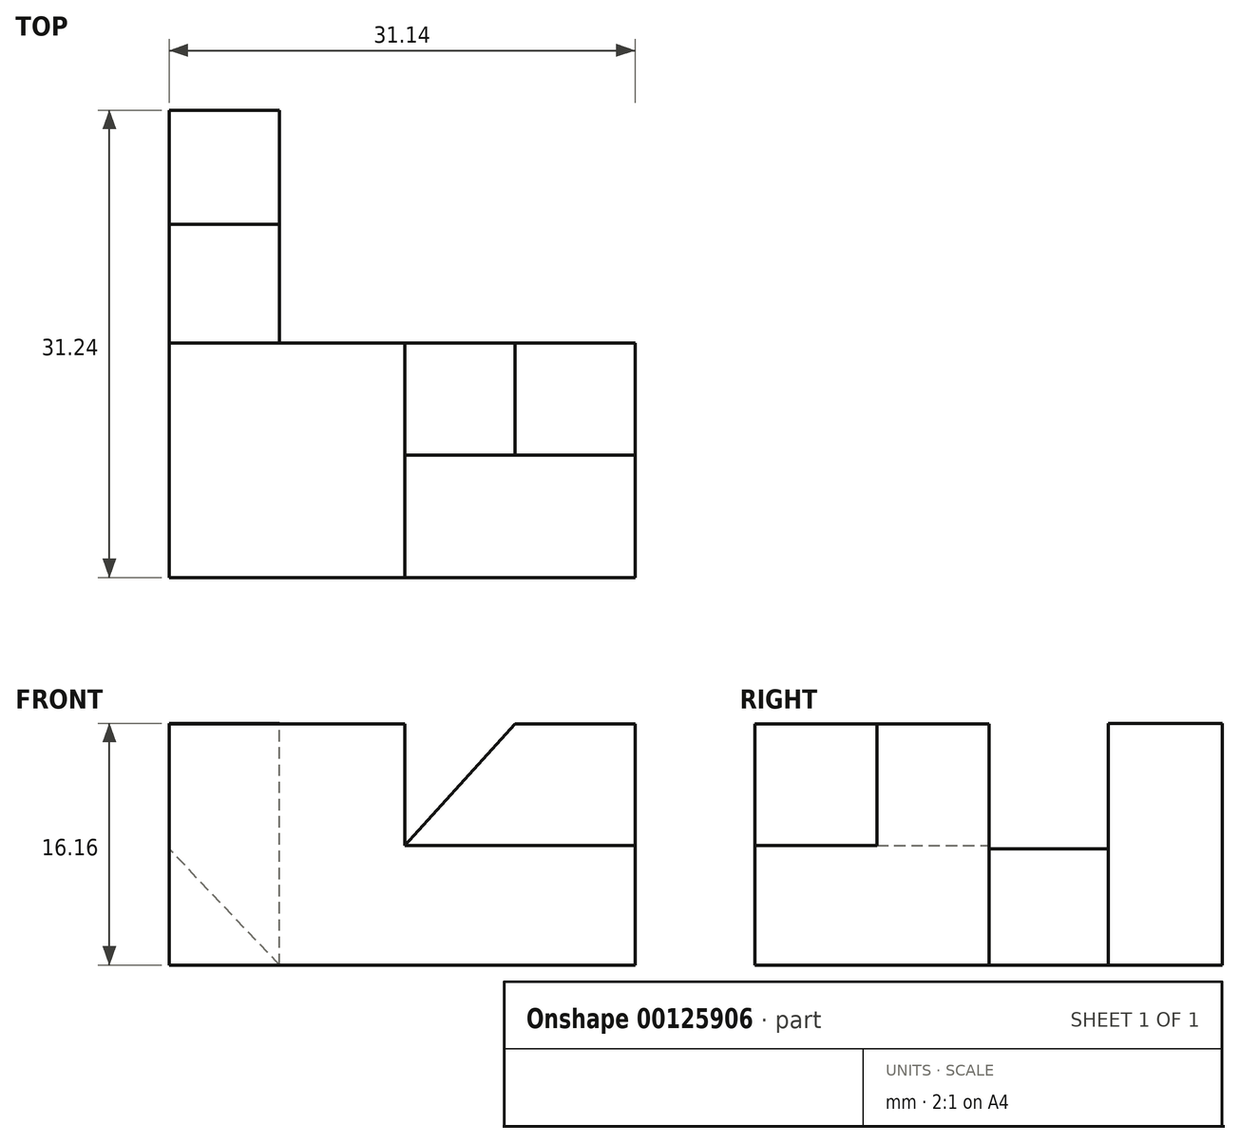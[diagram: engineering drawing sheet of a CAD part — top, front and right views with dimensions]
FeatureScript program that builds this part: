
annotation { "Feature Type Name" : "Feature", "Feature Type Description" : "" }
export const myFeature = defineFeature(function(context is Context, id is Id, definition is map)
    precondition{}
    {
        {
            var Q0;
            Q0=qCreatedBy(makeId("Front.planeOp"),FACE);
            var sketch = newSketch(context, id + "F0", { "sketchPlane" : qUnion([Q0])});
            skLineSegment(sketch, "E0.bottom", {"start": v(0, 0) * mm, "end": v(15.75, 0) * mm});
            skLineSegment(sketch, "E0.top", {"start": v(0, 16.1) * mm, "end": v(15.75, 16.1) * mm});
            skLineSegment(sketch, "E0.left", {"start": v(0, 0) * mm, "end": v(0, 16.1) * mm});
            skLineSegment(sketch, "E0.right", {"start": v(15.75, 0) * mm, "end": v(15.75, 16.1) * mm});
            skLineSegment(sketch, "E1.bottom", {"start": v(15.75, 0) * mm, "end": v(31.14, 0) * mm});
            skLineSegment(sketch, "E1.top", {"start": v(15.75, 8) * mm, "end": v(31.14, 8) * mm});
            skLineSegment(sketch, "E1.left", {"start": v(15.75, 0) * mm, "end": v(15.75, 8) * mm});
            skLineSegment(sketch, "E1.right", {"start": v(31.14, 0) * mm, "end": v(31.14, 8) * mm});
            skSolve(sketch);
        }
        {
            var Q0;
            Q0=makeQuery(id+"F0.imprint","IMPRINT",FACE,{"disambiguationData":[TD([[makeQuery(id+"F0.imprint","IMPRINT",EDGE,{"derivedFrom":sQuery(id+"F0.wireOp",EDGE,"E1.bottom")}),1.0]])]});
            var Q1;
            Q1=makeQuery(id+"F0.imprint","IMPRINT",FACE,{"disambiguationData":[TD([[makeQuery(id+"F0.imprint","IMPRINT",EDGE,{"derivedFrom":sQuery(id+"F0.wireOp",EDGE,"E0.bottom")}),1.0]])]});
            extrude(context, id + "F1", {"entities" : qUnion([Q0, Q1]), "depth" : 15.67 * mm});
        }
        {
            var Q0;
            Q0=makeQuery(id+"F1.opExtrude","CAP_FACE",FACE,{"disambiguationData":[OSD([sQuery(id+"F0.wireOp",EDGE,"E0.bottom"),sQuery(id+"F0.wireOp",EDGE,"E0.top"),sQuery(id+"F0.wireOp",EDGE,"E0.left"),sQuery(id+"F0.wireOp",EDGE,"E0.right"),sQuery(id+"F0.wireOp",EDGE,"E1.bottom"),sQuery(id+"F0.wireOp",EDGE,"E1.top"),sQuery(id+"F0.wireOp",EDGE,"E1.right")])],"isStart":true});
            var sketch = newSketch(context, id + "F2", { "sketchPlane" : qUnion([Q0])});
            skLineSegment(sketch, "E2", {"start": v(-31.14, 8) * mm, "end": v(-15.75, 8) * mm});
            skLineSegment(sketch, "E3", {"start": v(-15.75, 8) * mm, "end": v(-23.11, 16.1) * mm});
            skLineSegment(sketch, "E4", {"start": v(-23.11, 16.1) * mm, "end": v(-31.14, 16.1) * mm});
            skLineSegment(sketch, "E5", {"start": v(-31.14, 16.1) * mm, "end": v(-31.14, 8) * mm});
            skSolve(sketch);
        }
        {
            var Q0;
            Q0=makeQuery(id+"F2.imprint","IMPRINT",FACE,{"disambiguationData":[TD([[makeQuery(id+"F2.imprint","IMPRINT",EDGE,{"derivedFrom":sQuery(id+"F2.wireOp",EDGE,"E2")}),-1.0]])]});
            extrude(context, id + "F3", {"entities" : qUnion([Q0]), "operationType" : NewBodyOperationType.ADD, "oppositeDirection" : true, "depth" : 7.5 * mm});
        }
        {
            var Q0;
            Q0=makeQuery(id+"F3.boolean.opBoolean","MERGE",FACE,{"derivedFrom":[makeQuery(id+"F1.opExtrude","CAP_FACE",FACE,{"disambiguationData":[OSD([sQuery(id+"F0.wireOp",EDGE,"E0.bottom"),sQuery(id+"F0.wireOp",EDGE,"E0.top"),sQuery(id+"F0.wireOp",EDGE,"E0.left"),sQuery(id+"F0.wireOp",EDGE,"E0.right"),sQuery(id+"F0.wireOp",EDGE,"E1.bottom"),sQuery(id+"F0.wireOp",EDGE,"E1.top"),sQuery(id+"F0.wireOp",EDGE,"E1.right")])],"isStart":true}),makeQuery(id+"F3.opExtrude","CAP_FACE",FACE,{"disambiguationData":[OSD([sQuery(id+"F2.wireOp",EDGE,"E2"),sQuery(id+"F2.wireOp",EDGE,"E3"),sQuery(id+"F2.wireOp",EDGE,"E4"),sQuery(id+"F2.wireOp",EDGE,"E5")])],"isStart":true})]});
            var sketch = newSketch(context, id + "F4", { "sketchPlane" : qUnion([Q0])});
            skLineSegment(sketch, "E6", {"start": v(0, 0) * mm, "end": v(0, 7.77) * mm});
            skLineSegment(sketch, "E7", {"start": v(0, 0) * mm, "end": v(-7.37, 0) * mm});
            skLineSegment(sketch, "E8", {"start": v(-7.37, 0) * mm, "end": v(0, 7.77) * mm});
            skSolve(sketch);
        }
        {
            var Q0;
            Q0=makeQuery(id+"F4.imprint","IMPRINT",FACE,{"disambiguationData":[TD([[makeQuery(id+"F4.imprint","IMPRINT",EDGE,{"derivedFrom":sQuery(id+"F4.wireOp",EDGE,"E6")}),1.0]])]});
            extrude(context, id + "F5", {"entities" : qUnion([Q0]), "operationType" : NewBodyOperationType.ADD, "depth" : 7.95 * mm});
        }
        {
            var Q0;
            Q0=makeQuery(id+"F5.opExtrude","CAP_FACE",FACE,{"disambiguationData":[OSD([sQuery(id+"F4.wireOp",EDGE,"E6"),sQuery(id+"F4.wireOp",EDGE,"E7"),sQuery(id+"F4.wireOp",EDGE,"E8")])],"isStart":false});
            var sketch = newSketch(context, id + "F6", { "sketchPlane" : qUnion([Q0])});
            skLineSegment(sketch, "E9.bottom", {"start": v(0, 0) * mm, "end": v(-7.37, 0) * mm});
            skLineSegment(sketch, "E9.top", {"start": v(0, 16.16) * mm, "end": v(-7.37, 16.16) * mm});
            skLineSegment(sketch, "E9.left", {"start": v(0, 0) * mm, "end": v(0, 16.16) * mm});
            skLineSegment(sketch, "E9.right", {"start": v(-7.37, 0) * mm, "end": v(-7.37, 16.16) * mm});
            skSolve(sketch);
        }
        {
            var Q0;
            {var subQ0=sQuery(id+"F6.wireOp",EDGE,"E9.bottom");Q0=makeQuery(id+"F6.imprint","IMPRINT",FACE,{"disambiguationData":[TD([[makeQuery(id+"F6.imprint","IMPRINT",EDGE,{"derivedFrom":subQ0}),-1.0]])]});}
            var Q1;
            {var subQ0=sQuery(id+"F6.wireOp",EDGE,"E9.top");Q1=makeQuery(id+"F6.imprint","IMPRINT",FACE,{"disambiguationData":[TD([[makeQuery(id+"F6.imprint","IMPRINT",EDGE,{"derivedFrom":subQ0}),1.0]])]});}
            extrude(context, id + "F7", {"entities" : qUnion([Q0, Q1]), "operationType" : NewBodyOperationType.ADD, "depth" : 7.62 * mm});
        }
    });
